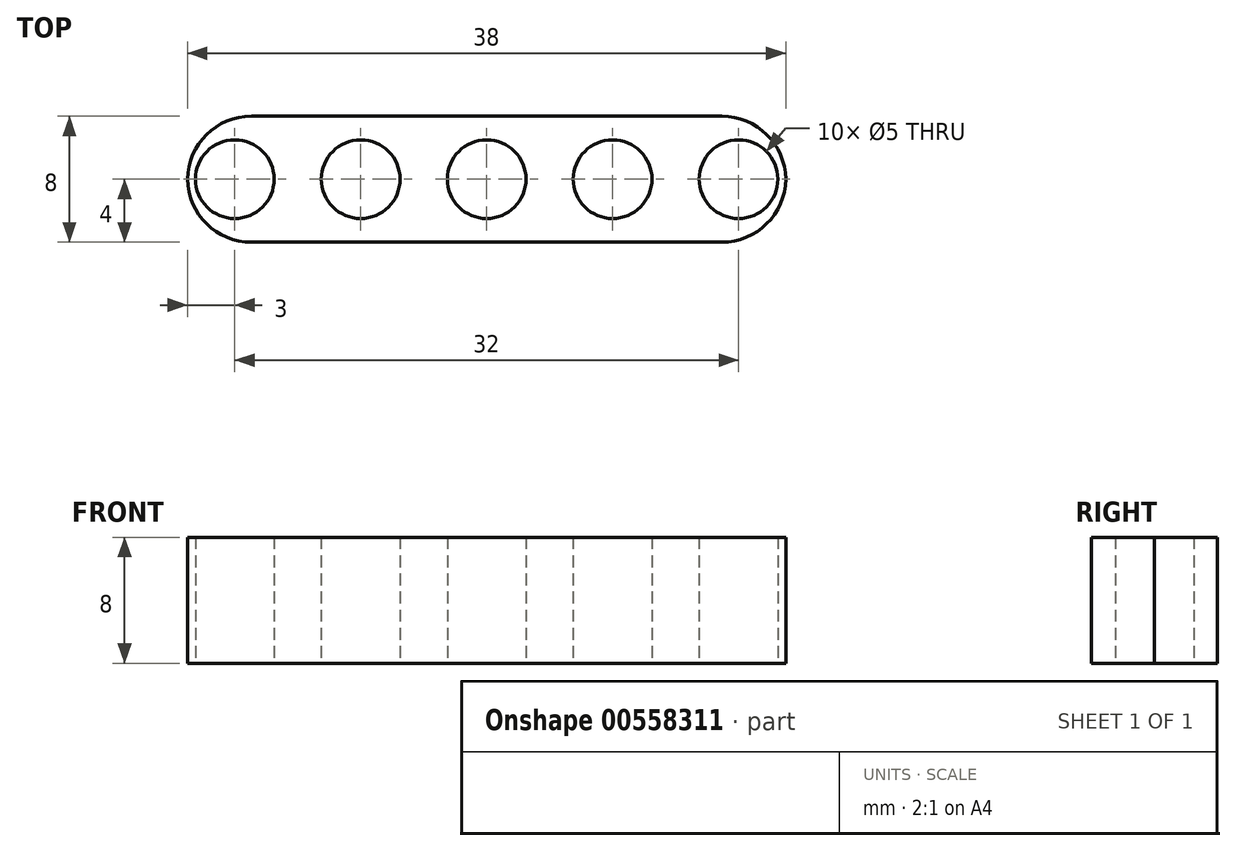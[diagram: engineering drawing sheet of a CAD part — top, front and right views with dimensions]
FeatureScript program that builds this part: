
annotation { "Feature Type Name" : "Feature", "Feature Type Description" : "" }
export const myFeature = defineFeature(function(context is Context, id is Id, definition is map)
    precondition{}
    {
        {
            var Q0;
            Q0=qCreatedBy(makeId("Top.planeOp"),FACE);
            var sketch = newSketch(context, id + "F0", { "sketchPlane" : qUnion([Q0])});
            skLineSegment(sketch, "E0.bottom", {"start": v(-19, 4) * mm, "end": v(19, 4) * mm});
            skLineSegment(sketch, "E0.top", {"start": v(-19, -4) * mm, "end": v(19, -4) * mm});
            skLineSegment(sketch, "E0.left", {"start": v(-19, 4) * mm, "end": v(-19, -4) * mm});
            skLineSegment(sketch, "E0.right", {"start": v(19, 4) * mm, "end": v(19, -4) * mm});
            skPoint(sketch, "E0.middle", {"position": v(0, 0) * mm});
            skCircle(sketch, "E1", {"center": v(0, 0) * mm, "radius": 2.5 * mm});
            skCircle(sketch, "E2.1.0.0", {"center": v(-8, 0) * mm, "radius": 2.5 * mm});
            skCircle(sketch, "E2.2.0.0", {"center": v(-16, 0) * mm, "radius": 2.5 * mm});
            skLineSegment(sketch, "E2.direction1", {"start": v(0, 0) * mm, "end": v(-8, 0) * mm, "construction": true});
            skCircle(sketch, "E3.1.0.0", {"center": v(8, 0) * mm, "radius": 2.5 * mm});
            skCircle(sketch, "E3.2.0.0", {"center": v(16, 0) * mm, "radius": 2.5 * mm});
            skLineSegment(sketch, "E3.direction1", {"start": v(0, 0) * mm, "end": v(8, 0) * mm, "construction": true});
            skLineSegment(sketch, "E4", {"start": v(-18.5, 0) * mm, "end": v(-13.5, 0) * mm});
            skPoint(sketch, "E4.startSnap0", {"position": v(-19, 0) * mm});
            skSolve(sketch);
        }
        {
            var Q0;
            Q0=makeQuery(id+"F0.imprint","IMPRINT",FACE,{"disambiguationData":[TD([[makeQuery(id+"F0.imprint","IMPRINT",EDGE,{"derivedFrom":sQuery(id+"F0.wireOp",EDGE,"E0.bottom")}),-1.0]])]});
            extrude(context, id + "F1", {"entities" : qUnion([Q0]), "depth" : 8 * mm, "offsetDistance" : 25.4 * mm});
        }
        {
            var Q0;
            Q0=makeQuery(id+"F1.opExtrude","SWEPT_EDGE",EDGE,{"disambiguationData":[OSD([sQuery(id+"F0.wireOp",EDGE,"E0.top"),sQuery(id+"F0.wireOp",EDGE,"E0.right")])]});
            var Q1;
            Q1=makeQuery(id+"F1.opExtrude","SWEPT_EDGE",EDGE,{"disambiguationData":[OSD([sQuery(id+"F0.wireOp",EDGE,"E0.bottom"),sQuery(id+"F0.wireOp",EDGE,"E0.right")])]});
            var Q2;
            Q2=makeQuery(id+"F1.opExtrude","SWEPT_EDGE",EDGE,{"disambiguationData":[OSD([sQuery(id+"F0.wireOp",EDGE,"E0.top"),sQuery(id+"F0.wireOp",EDGE,"E0.left")])]});
            var Q3;
            Q3=makeQuery(id+"F1.opExtrude","SWEPT_EDGE",EDGE,{"disambiguationData":[OSD([sQuery(id+"F0.wireOp",EDGE,"E0.bottom"),sQuery(id+"F0.wireOp",EDGE,"E0.left")])]});
            fillet(context, id + "F2", {"entities" : qUnion([Q0, Q1, Q2, Q3]), "radius" : 4.06 * mm, "tangentPropagation" : true, "allowEdgeOverflow" : false});
        }
    });
